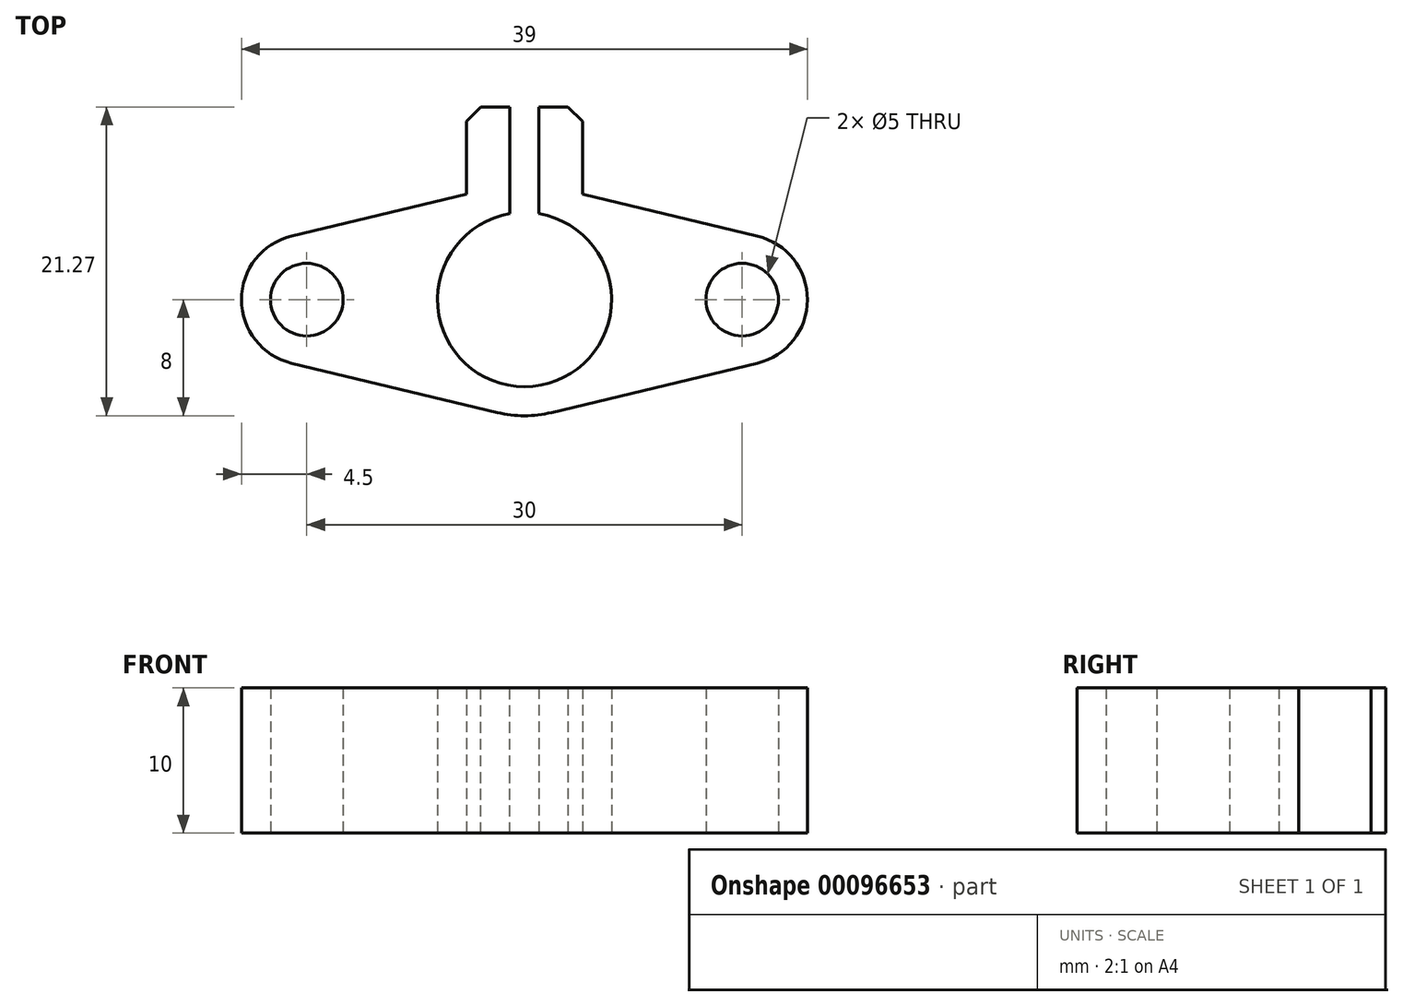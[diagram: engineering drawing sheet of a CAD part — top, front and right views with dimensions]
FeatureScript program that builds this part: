
annotation { "Feature Type Name" : "Feature", "Feature Type Description" : "" }
export const myFeature = defineFeature(function(context is Context, id is Id, definition is map)
    precondition{}
    {
        {
            var Q0;
            Q0=qCreatedBy(makeId("Top.planeOp"),FACE);
            var sketch = newSketch(context, id + "F0", { "sketchPlane" : qUnion([Q0])});
            skCircle(sketch, "E0", {"center": v(0, 0) * mm, "radius": 6 * mm});
            skCircle(sketch, "E1", {"center": v(-15, 0) * mm, "radius": 2.5 * mm});
            skCircle(sketch, "E2.MirrorC", {"center": v(15, 0) * mm, "radius": 2.5 * mm});
            skCircle(sketch, "E3", {"center": v(-15, 0) * mm, "radius": 4.5 * mm, "construction": true});
            skPoint(sketch, "E4", {"position": v(-19.5, 0) * mm});
            skPoint(sketch, "E5", {"position": v(-17.5, 0) * mm});
            skCircle(sketch, "E6", {"center": v(0, 0) * mm, "radius": 8 * mm, "construction": true});
            skPoint(sketch, "E7", {"position": v(-8, 0) * mm});
            skPoint(sketch, "E8", {"position": v(-6, 0) * mm});
            skLineSegment(sketch, "E9", {"start": v(-16.05, -4.38) * mm, "end": v(-1.87, -7.78) * mm});
            skArc(sketch, "E10", {"start": v(-16.05, -4.38) * mm, "mid": v(-19.5, 0) * mm, "end": v(-16.05, 4.38) * mm});
            skLineSegment(sketch, "E11", {"start": v(-16.05, 4.38) * mm, "end": v(-4, 7.27) * mm});
            skLineSegment(sketch, "E12", {"start": v(-4, 7.27) * mm, "end": v(-4, 13.27) * mm});
            skLineSegment(sketch, "E13", {"start": v(-4, 13.27) * mm, "end": v(0, 13.27) * mm});
            skArc(sketch, "E14", {"start": v(-1.87, -7.78) * mm, "mid": v(-0.94, -7.94) * mm, "end": v(0, -8) * mm});
            skLineSegment(sketch, "E15.MirrorCS", {"start": v(4, 13.27) * mm, "end": v(0, 13.27) * mm});
            skLineSegment(sketch, "E16.MirrorCS", {"start": v(4, 7.27) * mm, "end": v(4, 13.27) * mm});
            skLineSegment(sketch, "E17.MirrorCS", {"start": v(16.05, 4.38) * mm, "end": v(4, 7.27) * mm});
            skArc(sketch, "E18.MirrorCS", {"start": v(16.05, -4.38) * mm, "mid": v(19.5, 0) * mm, "end": v(16.05, 4.38) * mm});
            skLineSegment(sketch, "E19.MirrorCS", {"start": v(16.05, -4.38) * mm, "end": v(1.87, -7.78) * mm});
            skArc(sketch, "E20.MirrorCS", {"start": v(1.87, -7.78) * mm, "mid": v(0.94, -7.94) * mm, "end": v(0, -8) * mm});
            skSolve(sketch);
        }
        {
            var Q0;
            Q0 = qSketchRegion(id + "F0", true);
            extrude(context, id + "F1", {"entities" : qUnion([Q0]), "endBound" : BoundingType.SYMMETRIC, "depth" : 10 * mm});
        }
        {
            var Q0;
            Q0=makeQuery(id+"F1.opExtrude","SWEPT_FACE",FACE,{"disambiguationData":[OSD([sQuery(id+"F0.wireOp",EDGE,"E13"),sQuery(id+"F0.wireOp",EDGE,"E15.MirrorCS")])]});
            var sketch = newSketch(context, id + "F2", { "sketchPlane" : qUnion([Q0])});
            skLineSegment(sketch, "E21.bottom", {"start": v(1, -5) * mm, "end": v(-1, -5) * mm});
            skLineSegment(sketch, "E21.top", {"start": v(1, 5) * mm, "end": v(-1, 5) * mm});
            skLineSegment(sketch, "E21.left", {"start": v(1, -5) * mm, "end": v(1, 5) * mm});
            skLineSegment(sketch, "E21.right", {"start": v(-1, -5) * mm, "end": v(-1, 5) * mm});
            skPoint(sketch, "E21.middle", {"position": v(0, 0) * mm});
            skSolve(sketch);
        }
        {
            var Q0;
            Q0 = qSketchRegion(id + "F2", true);
            extrude(context, id + "F3", {"entities" : qUnion([Q0]), "operationType" : NewBodyOperationType.REMOVE, "endBound" : BoundingType.UP_TO_NEXT, "oppositeDirection" : true, "depth" : 25 * mm});
        }
        {
            var Q0;
            Q0=makeQuery(id+"F1.opExtrude","SWEPT_EDGE",EDGE,{"disambiguationData":[OSD([sQuery(id+"F0.wireOp",EDGE,"E12"),sQuery(id+"F0.wireOp",EDGE,"E13")])]});
            var Q1;
            Q1=makeQuery(id+"F1.opExtrude","SWEPT_EDGE",EDGE,{"disambiguationData":[OSD([sQuery(id+"F0.wireOp",EDGE,"E15.MirrorCS"),sQuery(id+"F0.wireOp",EDGE,"E16.MirrorCS")])]});
            chamfer(context, id + "F4", {"entities" : qUnion([Q0, Q1]), "width" : 1 * mm, "tangentPropagation" : true});
        }
    });
